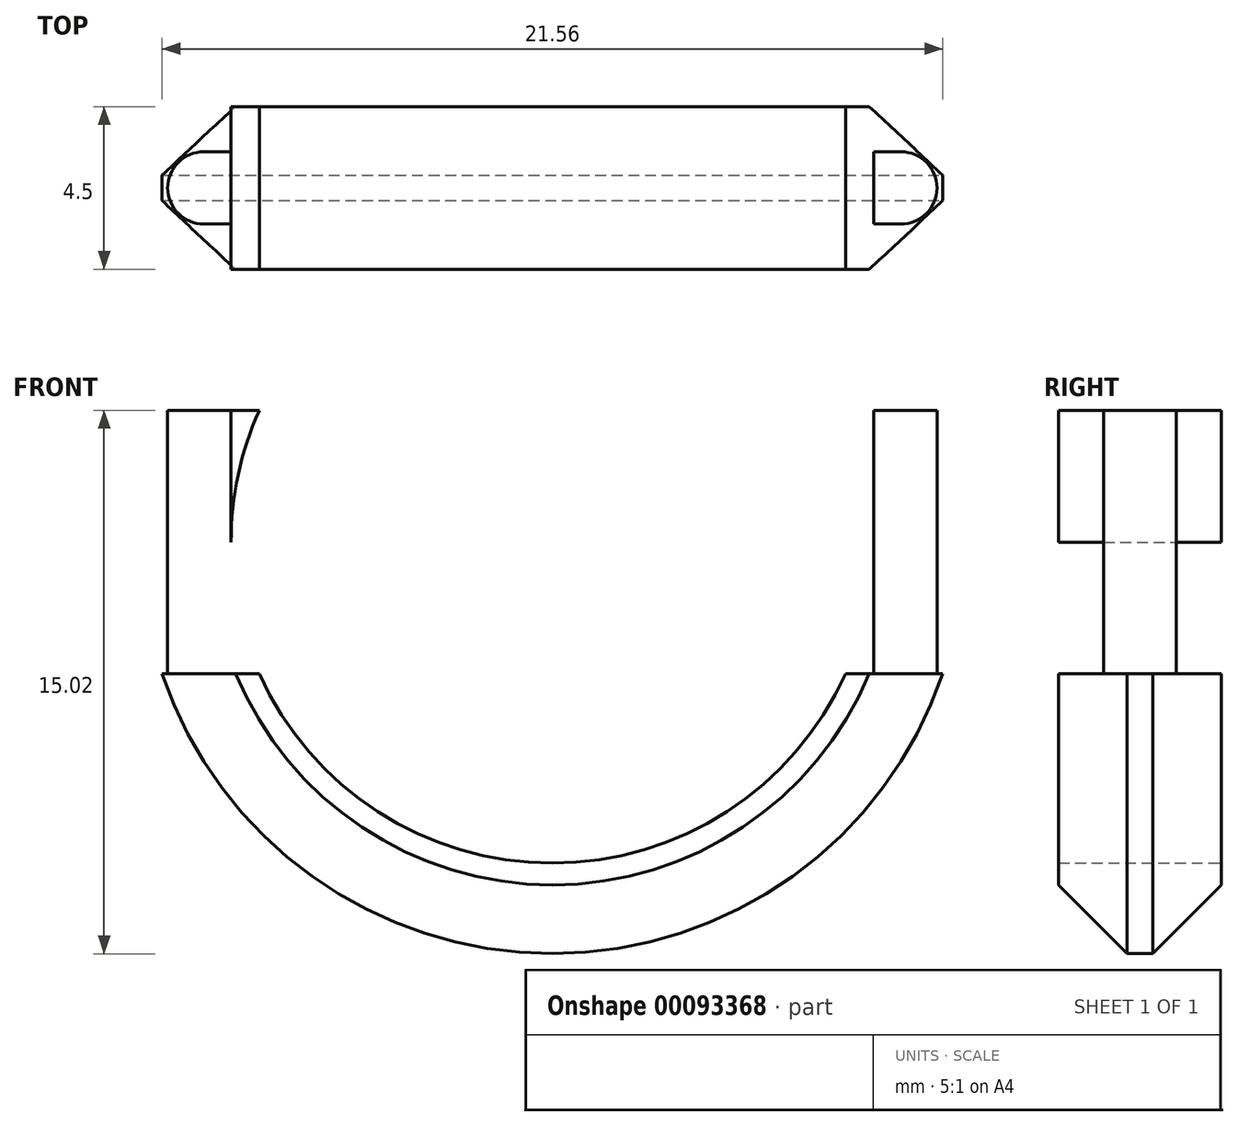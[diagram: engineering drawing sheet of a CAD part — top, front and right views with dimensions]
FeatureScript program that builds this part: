
annotation { "Feature Type Name" : "Feature", "Feature Type Description" : "" }
export const myFeature = defineFeature(function(context is Context, id is Id, definition is map)
    precondition{}
    {
        {
            var Q0;
            Q0=qCreatedBy(makeId("Front.planeOp"),FACE);
            var sketch = newSketch(context, id + "F0", { "sketchPlane" : qUnion([Q0])});
            skCircle(sketch, "E0", {"center": v(0, 0) * mm, "radius": 8.88 * mm});
            skCircle(sketch, "E1.0", {"center": v(0, 0) * mm, "radius": 11.38 * mm});
            skLineSegment(sketch, "E2", {"start": v(-10.78, 3.64) * mm, "end": v(10.78, 3.64) * mm});
            skLineSegment(sketch, "E3", {"start": v(-10.78, -3.64) * mm, "end": v(10.78, -3.64) * mm});
            skLineSegment(sketch, "E4", {"start": v(-8.88, 0) * mm, "end": v(-8.88, -3.64) * mm});
            skLineSegment(sketch, "E5", {"start": v(-8.88, -3.64) * mm, "end": v(-8.88, 3.64) * mm});
            skLineSegment(sketch, "E6", {"start": v(-10.62, 3.64) * mm, "end": v(-10.62, -3.64) * mm});
            skLineSegment(sketch, "E7.MirrorCS", {"start": v(8.88, -3.64) * mm, "end": v(8.88, 3.64) * mm});
            skLineSegment(sketch, "E8.MirrorCS", {"start": v(10.62, 3.64) * mm, "end": v(10.62, -3.64) * mm});
            skSolve(sketch);
        }
        {
            var Q0;
            {var subQ0=sQuery(id+"F0.wireOp",EDGE,"E2");var subQ6=sQuery(id+"F0.wireOp",EDGE,"E0");var subQ7=makeQuery(id+"F0.imprint","INTERSECT",VERTEX,{"disambiguationData":[OD(0.0)],"derivedFrom":[subQ6,subQ0]});Q0=makeQuery(id+"F0.imprint","IMPRINT",FACE,{"disambiguationData":[TD([[makeQuery(id+"F0.imprint","IMPRINT",EDGE,{"disambiguationData":[TD([[subQ7,-1.0]])],"derivedFrom":subQ6}),-1.0]])]});}
            var Q1;
            {var subQ0=sQuery(id+"F0.wireOp",EDGE,"E3");var subQ7=sQuery(id+"F0.wireOp",EDGE,"E0");var subQ9=makeQuery(id+"F0.imprint","INTERSECT",VERTEX,{"disambiguationData":[OD(0.0)],"derivedFrom":[subQ7,subQ0]});Q1=makeQuery(id+"F0.imprint","IMPRINT",FACE,{"disambiguationData":[TD([[makeQuery(id+"F0.imprint","IMPRINT",EDGE,{"disambiguationData":[TD([[subQ9,-1.0]])],"derivedFrom":subQ7}),-1.0]])]});}
            extrude(context, id + "F1", {"entities" : qUnion([Q0, Q1]), "depth" : 2.25 * mm, "hasSecondDirection" : true, "secondDirectionOppositeDirection" : true, "secondDirectionDepth" : 2.25 * mm});
        }
        {
            var Q0;
            {var subQ3=sQuery(id+"F0.wireOp",EDGE,"E8.MirrorCS");Q0=makeQuery(id+"F0.imprint","IMPRINT",FACE,{"disambiguationData":[TD([[makeQuery(id+"F0.imprint","IMPRINT",EDGE,{"derivedFrom":subQ3}),-1.0]])]});}
            var Q1;
            {var subQ3=sQuery(id+"F0.wireOp",EDGE,"E6");Q1=makeQuery(id+"F0.imprint","IMPRINT",FACE,{"disambiguationData":[TD([[makeQuery(id+"F0.imprint","IMPRINT",EDGE,{"derivedFrom":subQ3}),1.0]])]});}
            extrude(context, id + "F2", {"entities" : qUnion([Q0, Q1]), "depth" : 1 * mm, "hasSecondDirection" : true, "secondDirectionOppositeDirection" : true, "secondDirectionDepth" : 1 * mm});
        }
        {
            var Q0;
            {var subQ0=sQuery(id+"F0.wireOp",EDGE,"E2");var subQ1=sQuery(id+"F0.wireOp",EDGE,"E1.0");Q0=makeQuery(id+"F1.opExtrude","CAP_EDGE",EDGE,{"disambiguationData":[OSD([subQ1]),TDD([makeQuery(id+"F0.imprint","IMPRINT",EDGE,{"disambiguationData":[TD([[makeQuery(id+"F0.imprint","INTERSECT",VERTEX,{"disambiguationData":[OD(0.0)],"derivedFrom":[subQ1,subQ0]}),1.0]])],"derivedFrom":subQ1})])],"isStart":true});}
            var Q1;
            {var subQ0=sQuery(id+"F0.wireOp",EDGE,"E3");var subQ1=sQuery(id+"F0.wireOp",EDGE,"E1.0");Q1=makeQuery(id+"F1.opExtrude","CAP_EDGE",EDGE,{"disambiguationData":[OSD([subQ1]),TDD([makeQuery(id+"F0.imprint","IMPRINT",EDGE,{"disambiguationData":[TD([[makeQuery(id+"F0.imprint","INTERSECT",VERTEX,{"disambiguationData":[OD(0.0)],"derivedFrom":[subQ1,subQ0]}),-1.0]])],"derivedFrom":subQ1})])],"isStart":true});}
            var Q2;
            {var subQ0=sQuery(id+"F0.wireOp",EDGE,"E2");var subQ1=sQuery(id+"F0.wireOp",EDGE,"E1.0");Q2=makeQuery(id+"F1.opExtrude","CAP_EDGE",EDGE,{"disambiguationData":[OSD([subQ1]),TDD([makeQuery(id+"F0.imprint","IMPRINT",EDGE,{"disambiguationData":[TD([[makeQuery(id+"F0.imprint","INTERSECT",VERTEX,{"disambiguationData":[OD(0.0)],"derivedFrom":[subQ1,subQ0]}),1.0]])],"derivedFrom":subQ1})])],"isStart":false});}
            var Q3;
            {var subQ0=sQuery(id+"F0.wireOp",EDGE,"E3");var subQ1=sQuery(id+"F0.wireOp",EDGE,"E1.0");Q3=makeQuery(id+"F1.opExtrude","CAP_EDGE",EDGE,{"disambiguationData":[OSD([subQ1]),TDD([makeQuery(id+"F0.imprint","IMPRINT",EDGE,{"disambiguationData":[TD([[makeQuery(id+"F0.imprint","INTERSECT",VERTEX,{"disambiguationData":[OD(0.0)],"derivedFrom":[subQ1,subQ0]}),-1.0]])],"derivedFrom":subQ1})])],"isStart":false});}
            chamfer(context, id + "F3", {"entities" : qUnion([Q0, Q1, Q2, Q3]), "width" : 1.9 * mm, "tangentPropagation" : true});
        }
        {
            var Q0;
            Q0=makeQuery(id+"F2.opExtrude","CAP_EDGE",EDGE,{"disambiguationData":[OSD([sQuery(id+"F0.wireOp",EDGE,"E8.MirrorCS")])],"isStart":false});
            var Q1;
            Q1=makeQuery(id+"F2.opExtrude","CAP_EDGE",EDGE,{"disambiguationData":[OSD([sQuery(id+"F0.wireOp",EDGE,"E8.MirrorCS")])],"isStart":true});
            var Q2;
            Q2=makeQuery(id+"F2.opExtrude","CAP_EDGE",EDGE,{"disambiguationData":[OSD([sQuery(id+"F0.wireOp",EDGE,"E6")])],"isStart":true});
            var Q3;
            Q3=makeQuery(id+"F2.opExtrude","CAP_EDGE",EDGE,{"disambiguationData":[OSD([sQuery(id+"F0.wireOp",EDGE,"E6")])],"isStart":false});
            fillet(context, id + "F4", {"entities" : qUnion([Q0, Q1, Q2, Q3]), "radius" : 1 * mm, "tangentPropagation" : true, "allowEdgeOverflow" : false});
        }
    });
